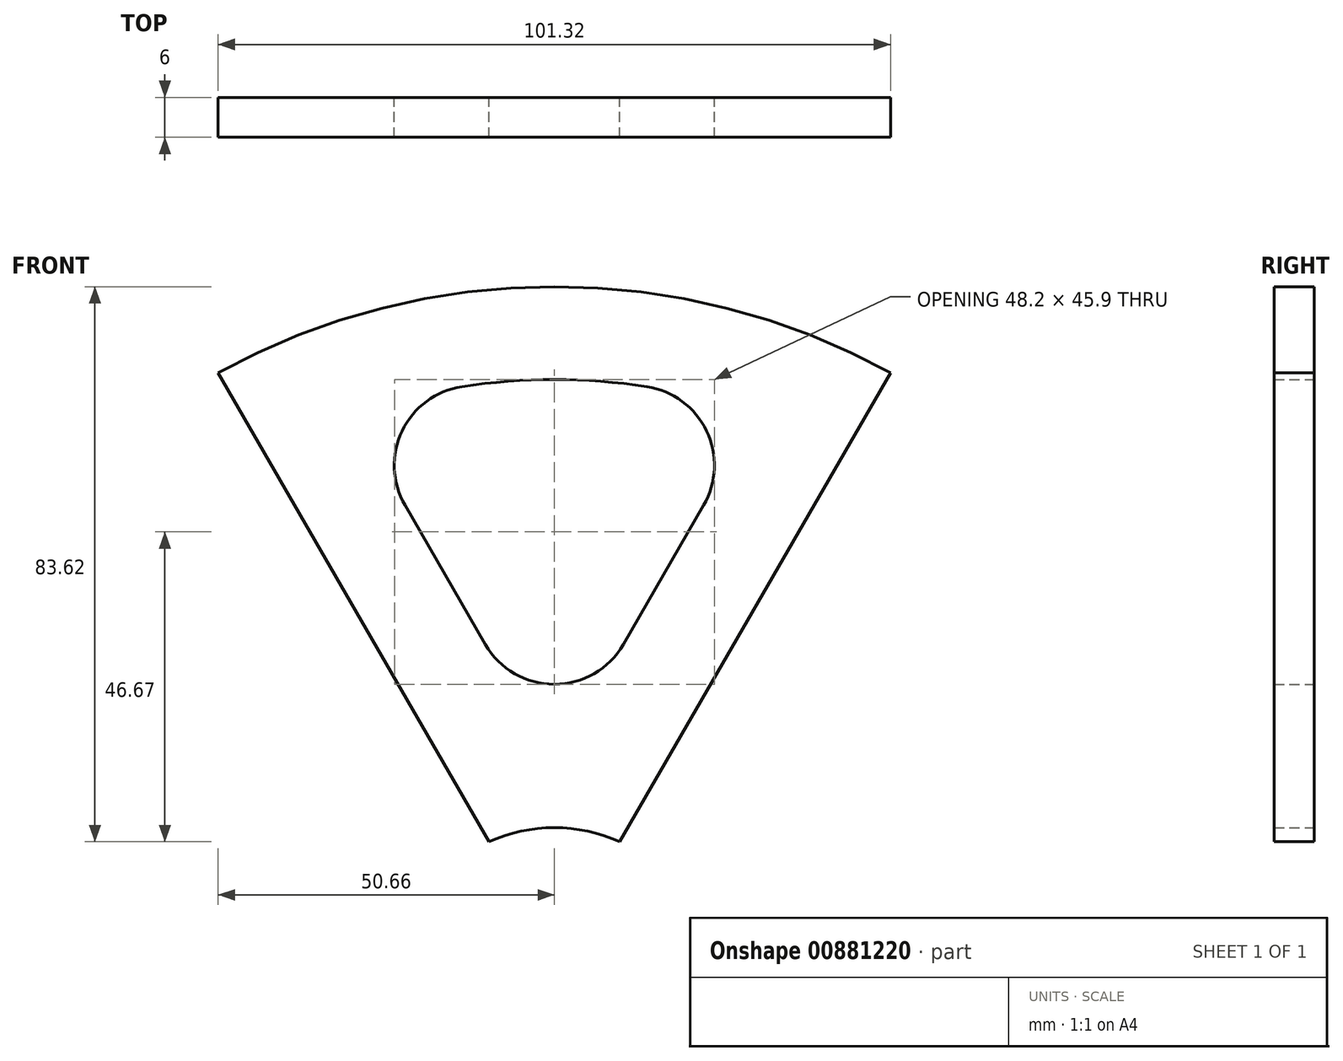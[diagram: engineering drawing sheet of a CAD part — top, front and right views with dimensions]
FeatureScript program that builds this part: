
annotation { "Feature Type Name" : "Feature", "Feature Type Description" : "" }
export const myFeature = defineFeature(function(context is Context, id is Id, definition is map)
    precondition{}
    {
        {
            var Q0;
            Q0=qCreatedBy(makeId("Front.planeOp"),FACE);
            var sketch = newSketch(context, id + "F0", { "sketchPlane" : qUnion([Q0])});
            skLineSegment(sketch, "E0", {"start": v(-50.66, 28.85) * mm, "end": v(-9.86, -41.8) * mm});
            skArc(sketch, "E1", {"start": v(9.86, -41.8) * mm, "mid": v(0, -39.7) * mm, "end": v(-9.86, -41.8) * mm});
            skLineSegment(sketch, "E2", {"start": v(50.66, 28.85) * mm, "end": v(9.86, -41.8) * mm});
            skArc(sketch, "E3", {"start": v(-10.4, -12.1) * mm, "mid": v(0, -18.1) * mm, "end": v(10.4, -12.1) * mm});
            skLineSegment(sketch, "E4", {"start": v(-22.5, 8.88) * mm, "end": v(-10.4, -12.1) * mm});
            skArc(sketch, "E5", {"start": v(-13.94, 26.74) * mm, "mid": v(-22.93, 20.07) * mm, "end": v(-22.5, 8.88) * mm});
            skArc(sketch, "E6", {"start": v(13.94, 26.74) * mm, "mid": v(0, 27.8) * mm, "end": v(-13.94, 26.74) * mm});
            skArc(sketch, "E7", {"start": v(22.5, 8.88) * mm, "mid": v(22.93, 20.07) * mm, "end": v(13.94, 26.74) * mm});
            skLineSegment(sketch, "E8", {"start": v(22.5, 8.88) * mm, "end": v(10.4, -12.1) * mm});
            skArc(sketch, "E9", {"start": v(50.66, 28.85) * mm, "mid": v(0, 41.8) * mm, "end": v(-50.66, 28.85) * mm});
            skSolve(sketch);
        }
        {
            var Q0;
            Q0 = qSketchRegion(id + "F0", true);
            extrude(context, id + "F1", {"entities" : qUnion([Q0]), "depth" : 6 * mm, "offsetDistance" : 25 * mm});
        }
    });
